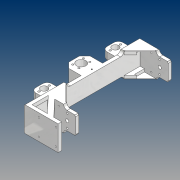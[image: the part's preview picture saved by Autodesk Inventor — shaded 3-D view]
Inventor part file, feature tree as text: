
AUTODESK INVENTOR PART (.ipt)
format: ipt  version: 2021 (Build 250183000, 183)  size: 493,568 bytes
history: native  units: mm
features: sketch x16, extrude x13, projected_geometry x12, fillet x3, mirror x3, chamfer x2, hole x2, other x2, reference x1
ambient origin geometry x8: Origin, YZ Plane, XZ Plane, XY Plane, X Axis, Y Axis, Z Axis, Center Point
bodies: Solid1 (feature_tree)
feature tree (54):
  extrude  "Extrusion1"  Depth=268.75mm
  extrude  "Extrusion2"  Depth=10.0mm
  extrude  "Extrusion3"  Depth=79.0mm TaperAngle=0.0deg
  fillet  "Fillet1"  Radius=45.0mm
  chamfer  "Chamfer1"  Distance=10.0mm
  mirror  "Mirror1"
  extrude  "Extrusion4"  Depth=2.0mm TaperAngle=45.0deg
  extrude  "Extrusion5"  Depth=36.5mm
  extrude  "Extrusion6"  TaperAngle=0.0deg  [1 undecoded]
  hole  "Hole2"  [1 undecoded]
  extrude  "Extrusion7"  Depth=10.0mm
  extrude  "Extrusion8"  Depth=55.5mm
  mirror  "Mirror2"
  extrude  "Extrusion9"  Depth=65.0mm
  hole  "Hole3"  [1 undecoded]
  sketch  "Sketch13"  dims[d41=47.35mm]
  extrude  "Extrusion10"  Depth=13.0mm
  chamfer  "Chamfer2"  Distance=10.0mm
  extrude  "Extrusion11"  Depth=50.0mm TaperAngle=0.0deg
  extrude  "Extrusion13"  Depth=20.0mm
  mirror  "Mirror5"
  fillet  "Fillet3"  Radius=5.0mm
  fillet  "Fillet4"  Radius=5.0mm
  extrude  "Extrusion14"  Depth=20.0mm
  sketch  "Sketch1"  dims[d0=50.0mm d1=268.75mm]
  sketch  "Sketch2"  dims[d2=10.0mm d3=0.0mm d5=250.0mm]
  projected_geometry  "Projected Loop1"
  sketch  "Sketch3"  dims[d6=251.0mm d7=79.0mm d8=0.0mm d9=45.0mm]
  projected_geometry  "Projected Loop2"
  sketch  "Sketch5"  dims[d10=45.0mm d11=10.0mm d12=0.0mm]
  sketch  "Sketch6"  dims[d13=10.0mm d14=2.0mm d15=2.0mm d16=45.0deg]
  projected_geometry  "Projected Loop3"
  sketch  "Sketch7"  dims[d26=36.5mm d27=5.2mm]
  projected_geometry  "Projected Loop4"
  sketch  "Sketch8"  dims[d28=9.0mm d29=0.0mm d30=0.0mm]
  sketch  "Sketch9"  dims[d31=65.0mm d32=10.0mm]
  projected_geometry  "Projected Loop5"
  sketch  "Sketch10"  dims[d33=10.0mm d34=40.0mm]
  projected_geometry  "Projected Loop6"
  sketch  "Sketch11"  dims[d35=55.5mm d36=0.0mm d37=55.0mm]
  projected_geometry  "Projected Loop7"
  sketch  "Sketch12"  dims[d38=10.0mm d39=0.0mm d40=65.0mm]
  projected_geometry  "Projected Loop8"
  sketch  "Sketch14"  dims[d42=4.2mm d43=6.0mm d44=4.0mm d45=2.0mm d46=90.0deg d47=8.0mm d48=20.594885mm d49=10.0mm]
  reference  "Reference4"
  sketch  "Sketch15"  dims[d50=144.0mm d51=0.0mm d52=13.0mm]
  projected_geometry  "Projected Loop9"
  projected_geometry  "Projected Loop10"
  sketch  "Sketch17"  dims[d53=43.0mm d54=10.0mm d55=0.0mm]
  projected_geometry  "Projected Loop13"
  sketch  "Sketch18"  dims[d56=60.0mm d57=50.0mm d58=0.0mm d59=40.0mm d60=26.0mm d61=6.0mm d62=4.0mm d63=2.0mm d64=90.0deg d65=12.5mm d66=20.594885mm d67=5.0mm d68=5.0mm d69=5.0mm d70=5.0mm d71=86.25mm d72=0.0mm d73=15.0mm d74=2.0mm d75=45.0deg d76=200.0mm d77=45.0mm d78=23.0mm d79=48.0mm d80=0.0mm d87=18.8mm d88=5.5mm d89=29.0mm d90=46.75mm d91=0.0mm d92=13.0mm d93=4.0mm d94=34.0mm d95=66.0mm d96=35.0mm d97=20.0mm d98=27.5mm d99=0.0mm]
  projected_geometry  "Projected Loop14"
  other  "0002_Part_Khop_tay_1.iam"
  other  "Dai_oc_truc_vit:1"
note: 3 required parameter values undecoded (feature->parameter linkage not recoverable at this tier; creation-order binding heuristic only, values carry confidence <= 0.55)
